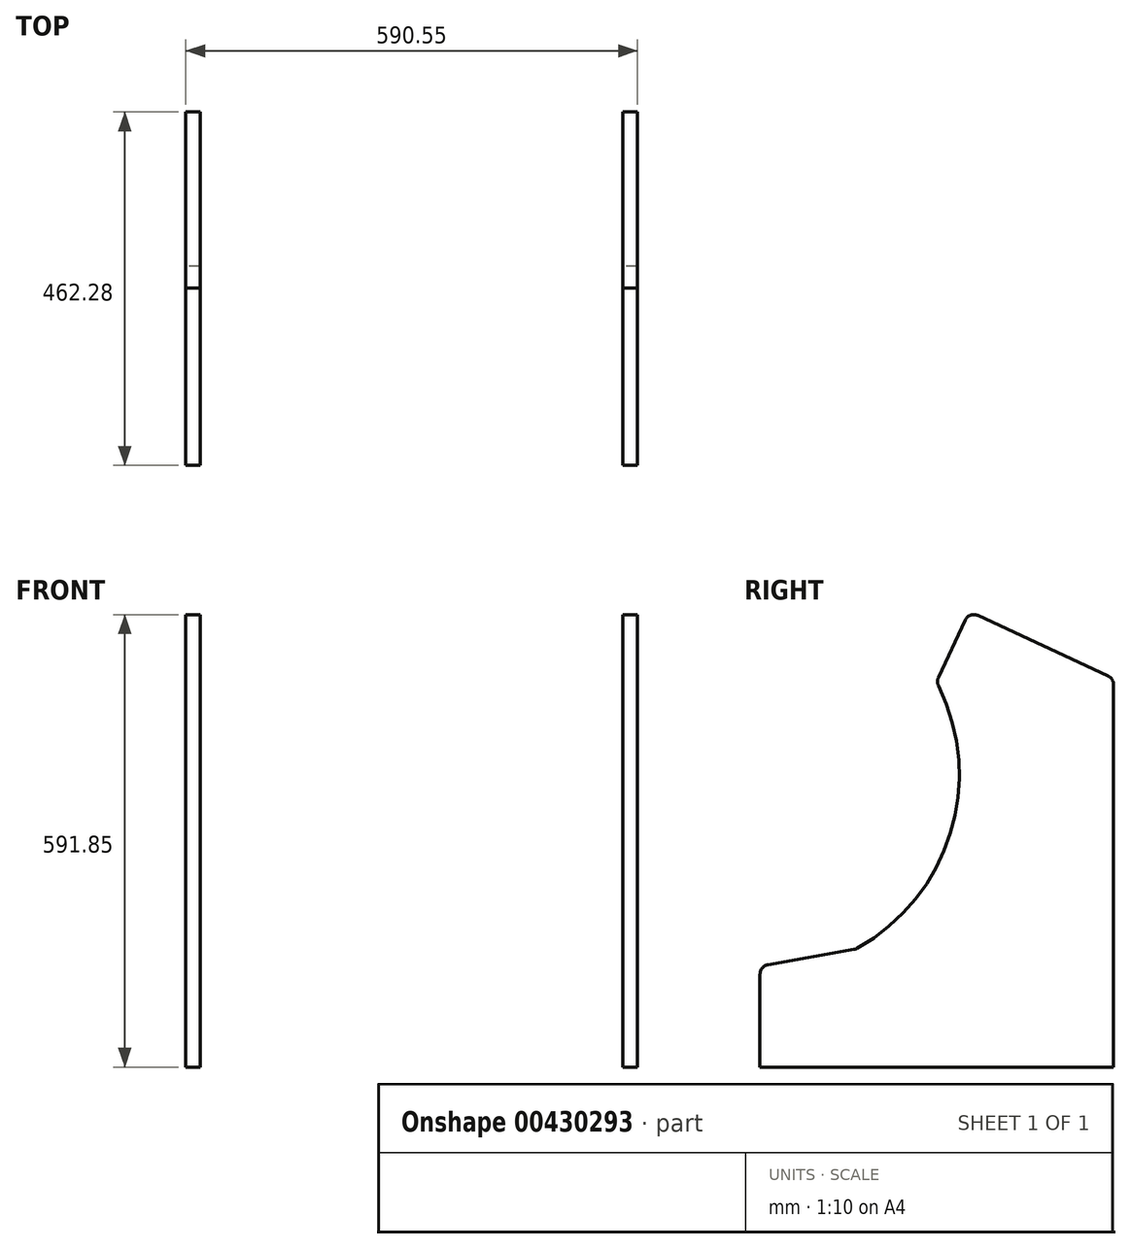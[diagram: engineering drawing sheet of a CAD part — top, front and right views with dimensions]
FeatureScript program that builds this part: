
annotation { "Feature Type Name" : "Feature", "Feature Type Description" : "" }
export const myFeature = defineFeature(function(context is Context, id is Id, definition is map)
    precondition{}
    {
        {
            var Q0;
            Q0=qCreatedBy(makeId("Right.planeOp"),FACE);
            var sketch = newSketch(context, id + "F0", { "sketchPlane" : qUnion([Q0])});
            skLineSegment(sketch, "E0", {"start": v(0, 499.9) * mm, "end": v(0, 0) * mm});
            skLineSegment(sketch, "E1.MirrorCS", {"start": v(-194.13, 584.51) * mm, "end": v(-229.08, 509.56) * mm});
            skLineSegment(sketch, "E2.MirrorCS", {"start": v(-462.28, 596.02) * mm, "end": v(-462.28, 132.08) * mm, "construction": true});
            skLineSegment(sketch, "E3.MirrorCS", {"start": v(-188.77, 596.02) * mm, "end": v(-462.28, 596.02) * mm, "construction": true});
            skLineSegment(sketch, "E4.MirrorCS", {"start": v(-7.33, 511.42) * mm, "end": v(-177.26, 590.66) * mm});
            skLineSegment(sketch, "E5", {"start": v(0, 0) * mm, "end": v(-462.28, 0) * mm});
            skLineSegment(sketch, "E6", {"start": v(-462.28, 0) * mm, "end": v(-462.28, 121.42) * mm});
            skLineSegment(sketch, "E7", {"start": v(-231.7, 503.94) * mm, "end": v(-231.7, 596.02) * mm, "construction": true});
            skLineSegment(sketch, "E8", {"start": v(-451.79, 133.93) * mm, "end": v(-339.3, 153.77) * mm});
            skArc(sketch, "E9", {"start": v(-335.3, 155.18) * mm, "mid": v(-213.42, 305.58) * mm, "end": v(-228.95, 498.55) * mm});
            skPoint(sketch, "E10.visualSharp", {"position": v(-462.28, 132.08) * mm});
            skArc(sketch, "E10.filletArc", {"start": v(-451.79, 133.93) * mm, "mid": v(-459.3, 129.59) * mm, "end": v(-462.28, 121.42) * mm});
            skPoint(sketch, "E11.visualSharp", {"position": v(-337.2, 154.13) * mm});
            skArc(sketch, "E11.filletArc", {"start": v(-339.3, 153.77) * mm, "mid": v(-337.24, 154.3) * mm, "end": v(-335.3, 155.18) * mm});
            skPoint(sketch, "E12.visualSharp", {"position": v(-231.7, 503.94) * mm});
            skArc(sketch, "E12.filletArc", {"start": v(-229.08, 509.56) * mm, "mid": v(-230.27, 504.04) * mm, "end": v(-228.95, 498.55) * mm});
            skPoint(sketch, "E13.visualSharp", {"position": v(-188.77, 596.02) * mm});
            skArc(sketch, "E13.filletArc", {"start": v(-177.26, 590.66) * mm, "mid": v(-186.97, 591.08) * mm, "end": v(-194.13, 584.51) * mm});
            skPoint(sketch, "E14.visualSharp", {"position": v(0, 508) * mm});
            skArc(sketch, "E14.filletArc", {"start": v(0, 499.9) * mm, "mid": v(-1.99, 506.73) * mm, "end": v(-7.33, 511.42) * mm});
            skSolve(sketch);
        }
        {
            var Q0;
            Q0 = qSketchRegion(id + "F0", true);
            extrude(context, id + "F1", {"entities" : qUnion([Q0]), "depth" : 19.05 * mm});
        }
        {
            var Q0;
            Q0=makeQuery(id+"F1.opExtrude","SWEPT_BODY",BODY,{"disambiguationData":[OSD([sQuery(id+"F0.wireOp",EDGE,"E0"),sQuery(id+"F0.wireOp",EDGE,"E1.MirrorCS"),sQuery(id+"F0.wireOp",EDGE,"E4.MirrorCS"),sQuery(id+"F0.wireOp",EDGE,"E5"),sQuery(id+"F0.wireOp",EDGE,"E6"),sQuery(id+"F0.wireOp",EDGE,"6ce56614-1373-4aa3-ab08-7f8a37f793d1")])]});
            transform(context, id + "F2", {"entities" : qUnion([Q0]), "transformType" : TransformType.TRANSLATION_3D, "dx" : 571.5 * mm, "dy" : 0 * mm, "dz" : 0 * mm, "makeCopy" : true});
        }
    });
